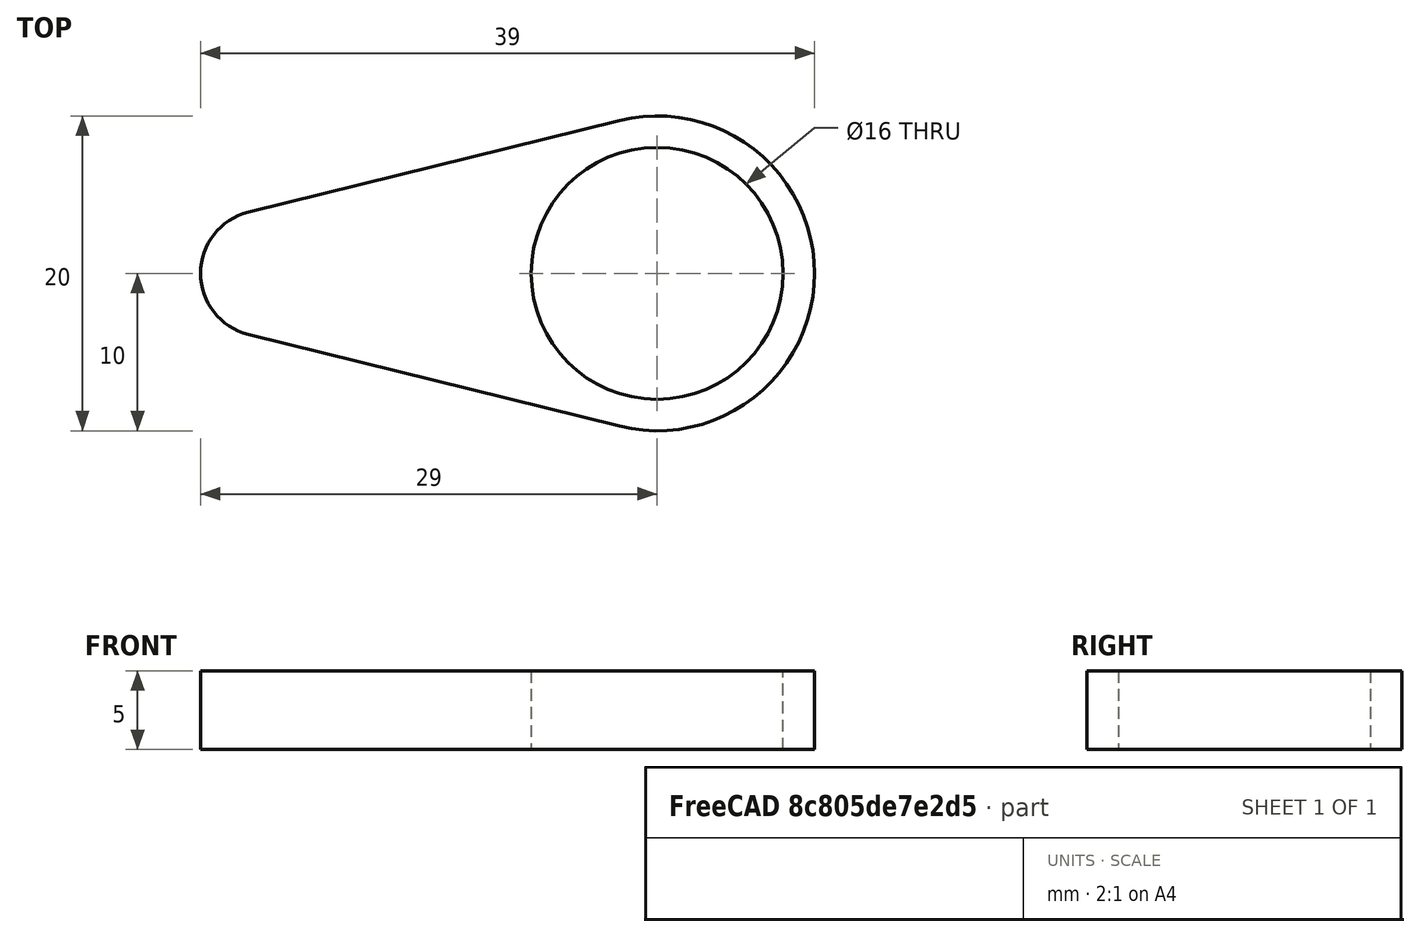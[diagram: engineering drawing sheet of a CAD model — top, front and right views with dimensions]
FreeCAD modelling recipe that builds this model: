
FCSTD DOCUMENT  (FreeCAD 0.19R24276 (Git))
Label: Knife_fork_part_2
License: All rights reserved
LicenseURL: http://en.wikipedia.org/wiki/All_rights_reserved
objects: Sketcher::SketchObject×1, PartDesign::Pad×1, PartDesign::Body×1
note: 4 computed .brp shape members not serialized (recipe doc carries the construction recipe); baked Part::Feature solids carry a one-line shape summary decoded from their .brp

FEATURE [Sketcher::SketchObject] Sketch
  FullyConstrained = true
  MapMode = 5
  Support = -> [XY_Plane]
  sketch-geometry (11):
    g0: Circle CenterX=0 CenterY=0 CenterZ=0 NormalX=0 NormalY=0 NormalZ=1 AngleXU=0 Radius=8
    g1: ArcOfCircle CenterX=0 CenterY=0 CenterZ=0 NormalX=0 NormalY=0 NormalZ=1 AngleXU=0 Radius=10 StartAngle=4.47002 EndAngle=8.09635
    g2: LineSegment StartX=0 StartY=0 StartZ=0 EndX=-25 EndY=0 EndZ=0
    g3: ArcOfCircle CenterX=-25 CenterY=0 CenterZ=0 NormalX=0 NormalY=0 NormalZ=1 AngleXU=0 Radius=4 StartAngle=1.81316 EndAngle=4.47002
    g4: LineSegment StartX=-25.96 StartY=3.88309 StartZ=0 EndX=-2.4 EndY=9.70773 EndZ=0
    g5: LineSegment StartX=-25.96 StartY=3.88309 StartZ=0 EndX=-25 EndY=0 EndZ=0
    g6: LineSegment StartX=-2.4 StartY=-9.70773 StartZ=0 EndX=-25.96 EndY=-3.88309 EndZ=0
    g7: LineSegment StartX=0 StartY=0 StartZ=0 EndX=-2.4 EndY=-9.70773 EndZ=0
    g8: LineSegment StartX=-25 StartY=0 StartZ=0 EndX=-25.96 EndY=-3.88309 EndZ=0
    g9: LineSegment StartX=0 StartY=0 StartZ=0 EndX=-2.4 EndY=9.70773 EndZ=0
    g10: Circle CenterX=-25 CenterY=0 CenterZ=0 NormalX=0 NormalY=0 NormalZ=1 AngleXU=0 Radius=4
  constraints (26):
    c: Coincident(g0,g-1)
    c: Diameter(g0) = 16
    c: Coincident(g1,g0)
    c: Diameter(g1) = 20
    c: Coincident(g2,g0)
    c: PointOnObject(g2,g-1)
    c: DistanceX(g2,g2) = 25
    c: Coincident(g3,g2)
    c: Diameter(g3) = 8
    c: Coincident(g5,g4)
    c: Coincident(g5,g2)
    c: Perpendicular(g5,g4)
    c: Coincident(g7,g0)
    c: Coincident(g7,g6)
    c: Perpendicular(g7,g6)
    c: Coincident(g8,g2)
    c: Coincident(g8,g6)
    c: Perpendicular(g6,g8)
    c: Coincident(g9,g0)
    c: Coincident(g9,g4)
    c: Coincident(g3,g4)
    c: Coincident(g3,g6)
    c: Tangent(g1,g4) = 1.5708
    c: Coincident(g1,g6)
    c: Coincident(g10,g3)
    c: Diameter(g10) = 8
FEATURE [PartDesign::Pad] Pad
  Direction = (1,1,1)
  Length = 5
  Length2 = 100
  Profile = -> Sketch
  Type = 0
FEATURE [PartDesign::Body] Body
  Group = -> [Sketch,Pad]
  Origin = -> Origin
  Tip = -> Pad
